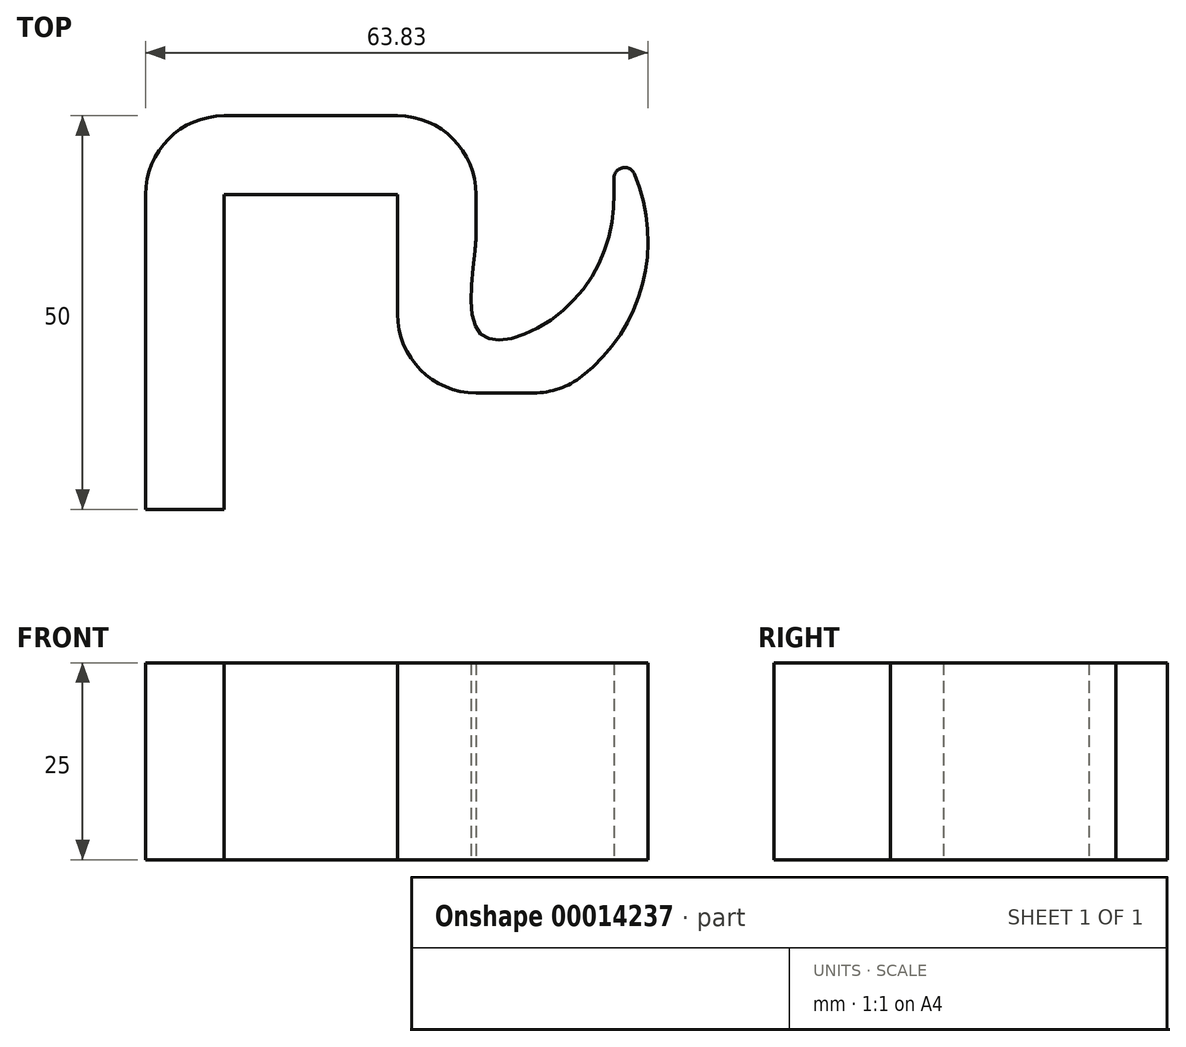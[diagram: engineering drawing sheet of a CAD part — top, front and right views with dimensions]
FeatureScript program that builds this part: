
annotation { "Feature Type Name" : "Feature", "Feature Type Description" : "" }
export const myFeature = defineFeature(function(context is Context, id is Id, definition is map)
    precondition{}
    {
        {
            var Q0;
            Q0=qCreatedBy(makeId("Top.planeOp"),FACE);
            var sketch = newSketch(context, id + "F0", { "sketchPlane" : qUnion([Q0])});
            skLineSegment(sketch, "E0.bottom", {"start": v(-12.3, -26.61) * mm, "end": v(9.7, -26.61) * mm});
            skLineSegment(sketch, "E0.left", {"start": v(-12.3, -26.61) * mm, "end": v(-12.3, -66.61) * mm});
            skLineSegment(sketch, "E0.right", {"start": v(9.7, -26.61) * mm, "end": v(9.7, -41.81) * mm});
            skLineSegment(sketch, "E1.0", {"start": v(-22.3, -26.61) * mm, "end": v(-22.3, -66.61) * mm});
            skLineSegment(sketch, "E1.1", {"start": v(-12.3, -16.61) * mm, "end": v(9.7, -16.61) * mm});
            skLineSegment(sketch, "E1.2", {"start": v(19.7, -26.61) * mm, "end": v(19.7, -31.24) * mm});
            skLineSegment(sketch, "E2", {"start": v(-22.3, -66.61) * mm, "end": v(-12.3, -66.61) * mm});
            skLineSegment(sketch, "E3", {"start": v(19.7, -51.81) * mm, "end": v(27, -51.81) * mm});
            skArc(sketch, "E4", {"start": v(33.17, -49.68) * mm, "mid": v(40.84, -37.98) * mm, "end": v(39.83, -24.03) * mm});
            skPoint(sketch, "E5.orphan", {"position": v(59.64, 0) * mm});
            skFitSpline(sketch, "E6", {"points": [v(36.64, -18.72) * mm, v(36.64, -31.71) * mm, v(29.36, -42.42) * mm, v(20.5, -44.5) * mm, v(19.7, -32.5) * mm], "startDerivative": vector(5.83, -50.3) * mm, "endDerivative": vector(7.83, 61.49) * mm});
            skArc(sketch, "E7.filletArc", {"start": v(19.55, -33.71) * mm, "mid": v(19.67, -32.48) * mm, "end": v(19.7, -31.24) * mm});
            skPoint(sketch, "E8.visualSharp", {"position": v(19.7, -16.61) * mm});
            skArc(sketch, "E8.filletArc", {"start": v(19.7, -26.61) * mm, "mid": v(16.78, -19.54) * mm, "end": v(9.7, -16.61) * mm});
            skPoint(sketch, "E9.visualSharp", {"position": v(-22.3, -16.61) * mm});
            skArc(sketch, "E9.filletArc", {"start": v(-12.3, -16.61) * mm, "mid": v(-19.36, -19.54) * mm, "end": v(-22.3, -26.61) * mm});
            skPoint(sketch, "E10.visualSharp", {"position": v(29.89, -51.81) * mm});
            skArc(sketch, "E10.filletArc", {"start": v(27, -51.81) * mm, "mid": v(30.27, -51.27) * mm, "end": v(33.17, -49.68) * mm});
            skPoint(sketch, "E11.visualSharp", {"position": v(9.7, -51.81) * mm});
            skArc(sketch, "E11.filletArc", {"start": v(9.7, -41.81) * mm, "mid": v(12.64, -48.88) * mm, "end": v(19.7, -51.81) * mm});
            skArc(sketch, "E12.filletArc", {"start": v(39.83, -24.03) * mm, "mid": v(38.26, -23.22) * mm, "end": v(37.2, -24.62) * mm});
            skSolve(sketch);
        }
        {
            var Q0;
            Q0 = qSketchRegion(id + "F0", true);
            extrude(context, id + "F1", {"entities" : qUnion([Q0]), "depth" : 25 * mm});
        }
    });
